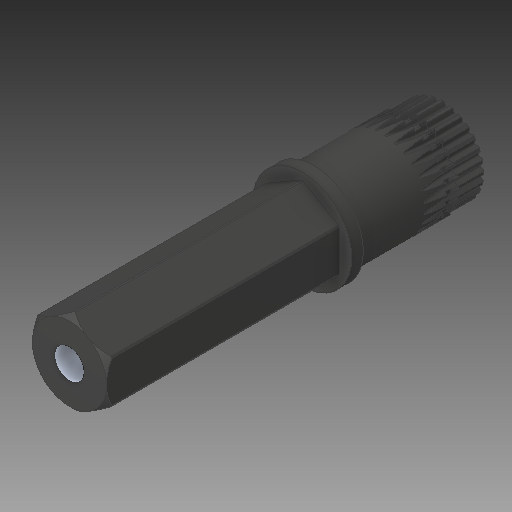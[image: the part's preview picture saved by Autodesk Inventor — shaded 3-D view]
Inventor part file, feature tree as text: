
AUTODESK INVENTOR PART (.ipt)
format: ipt  version: 2017 (Build 210142000, 142)  size: 1,395,712 bytes
history: native  units: in
note: dims shown in document units (in); Inventor stores cm internally (conversion verified against a paired STEP export)
features: fillet x1
ambient origin geometry x8: Origin, YZ Plane, XZ Plane, XY Plane, X Axis, Y Axis, Z Axis, Center Point
bodies: Solid1 (feature_tree)
feature tree (1):
  fillet  "Fillet5"  [1 undecoded]
note: 1 required parameter value undecoded (feature->parameter linkage not recoverable at this tier; creation-order binding heuristic only, values carry confidence <= 0.55)
